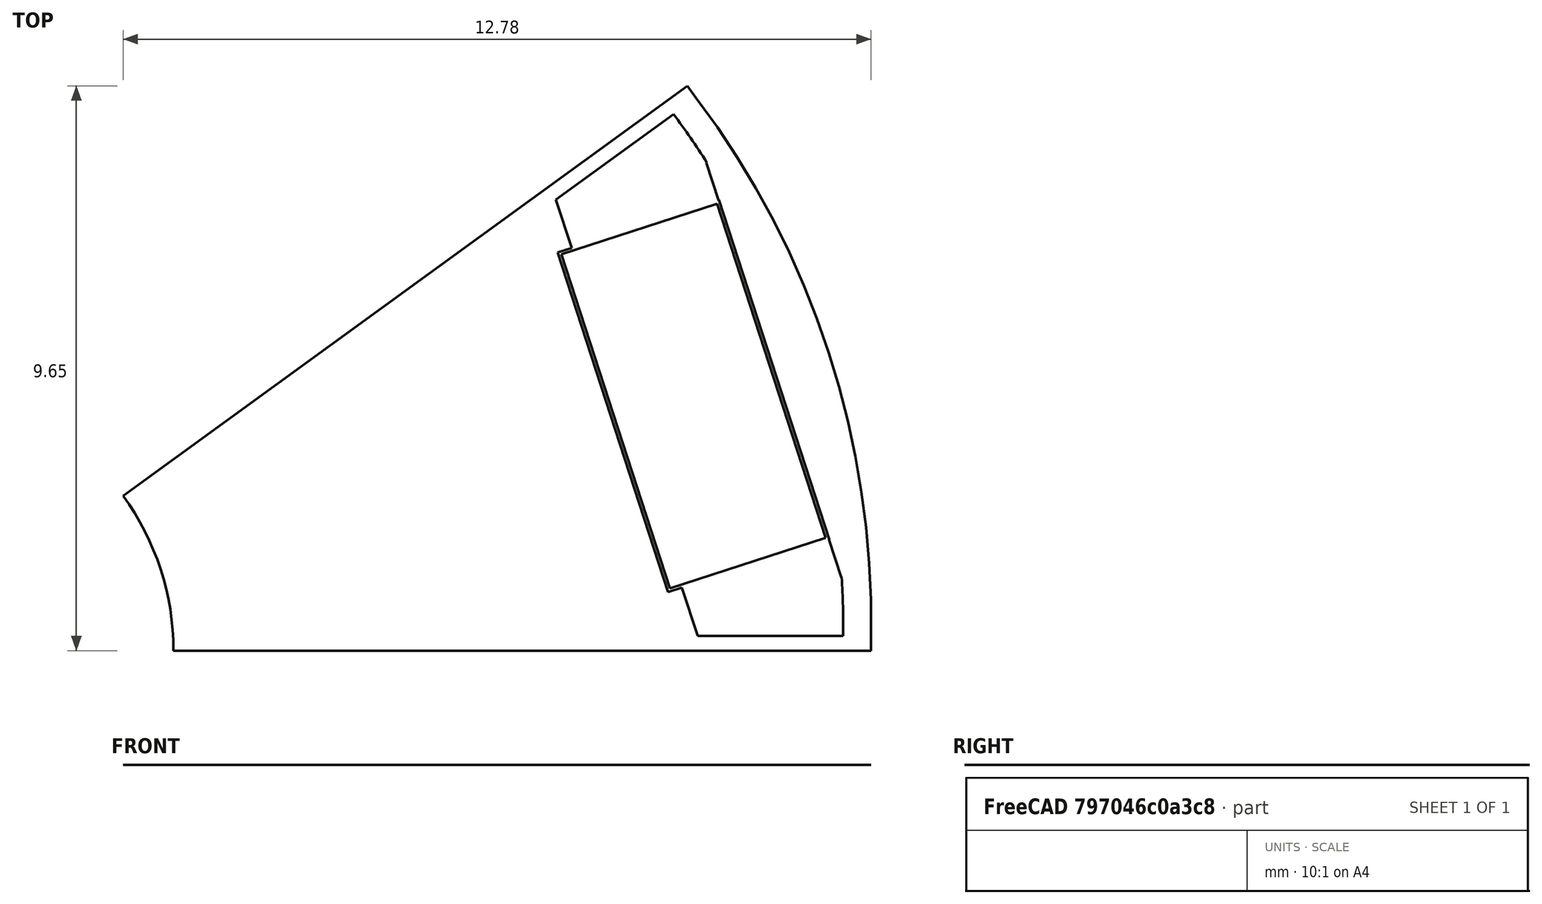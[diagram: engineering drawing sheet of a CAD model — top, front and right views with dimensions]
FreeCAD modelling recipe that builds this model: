
FCSTD DOCUMENT  (FreeCAD 0.18R4 (GitTag))
Label: rotor1
License: All rights reserved
LicenseURL: http://en.wikipedia.org/wiki/All_rights_reserved
objects: Sketcher::SketchObject×6, Surface::Filling×3, PartDesign::Body×2, Spreadsheet::Sheet×1, Part::Cut×1
note: 12 computed .brp shape members not serialized (recipe doc carries the construction recipe); baked Part::Feature solids carry a one-line shape summary decoded from their .brp

FEATURE [Spreadsheet::Sheet] Spreadsheet  label="Variables"
  cells = A2=poleNumber; B2(poleNumber)=10; A3=outerDiameter; B3(outerDiameter)=33; D3=Calc Value; A4=innerDiameter; B4(innerDiameter)=9; D4=Input Value; A5=stackLength; B5(stackLength)=20; A6=stackingFactor; B6(stackingFactor)=0.95; A7=embrace; B7(embrace)=75; A8=contourRatio; B8(contourRatio)=90; A9=magnetAirgap; B9(magnetAirgap)=0.05; A10=poleSeparation; B10(poleSeparation)=0.5; A11=magnetWidth; B11(magnetWidth)=6; A12=magnetHeight; B12(magnetHeight)=2.8; A13=rib; B13(rib)=0.5; A14=bridgeCurved; B14(bridgeCurved)=0.5; A15=cutTop; B15(cutTop)=0.01; A16=cutBottom; B16(cutBottom)=0.25; A17=segmentAngle; B17(segmentAngle)==360 / poleNumber; A18=movePocketInwards; B18(movePocketInwards)=0.01; A19=cuttingThickness; B19(cuttingThickness)=0.1; A20=magnetLength; B20(magnetLength)==stackLength; A21=cut; B21(cut)=0.2; A22=ribShaft; B22(ribShaft)=0.5; A23=magnetEmbrace; B23(magnetEmbrace)=70; A24=magnetContourRatio; B24(magnetContourRatio)=95; A25=axialMisalignment; B25(axialMisalignment)=0.5
FEATURE [Sketcher::SketchObject] Sketch003  label="RotorPoleSketch"
  MapMode = 5
  Support = -> [XY_Plane]
  expr: Constraints[14] = Variables.innerDiameter / 2
  expr: Constraints[55] = Variables.outerDiameter / 2 * Variables.contourRatio / 100
  expr: Constraints[73] = Variables.movePocketInwards
  expr: Constraints[59] = Variables.poleSeparation / 2
  expr: Constraints[106] = Variables.magnetHeight + 2 * Variables.magnetAirgap
  expr: Constraints[23] = Variables.outerDiameter / 2 * Variables.contourRatio / 100
  expr: Constraints[90] = Variables.cutTop
  expr: Constraints[71] = Variables.segmentAngle * Variables.embrace / 100
  expr: Constraints[15] = Variables.outerDiameter / 2
  expr: Constraints[103] = Variables.cutBottom
  expr: Constraints[58] = Variables.bridgeCurved
  expr: Constraints[114] = Variables.outerDiameter / 2 * Variables.contourRatio / 100 - Variables.bridgeCurved
  expr: Constraints[51] = Variables.rib / 2
  expr: Constraints[43] = Variables.rib / 2
  expr: Constraints[0] = Variables.segmentAngle
  expr: Constraints[18] = Variables.segmentAngle / 2
  expr: Constraints[91] = Variables.magnetWidth + Variables.magnetAirgap * 2
  expr: Constraints[116] = Variables.outerDiameter / 2 * Variables.contourRatio / 100 - Variables.bridgeCurved
  expr: Constraints[27] = Variables.poleSeparation / 2
  sketch-geometry (40):
    g0: LineSegment [constr] StartX=4.5 StartY=0 StartZ=0 EndX=16.5 EndY=0 EndZ=0
    g1: LineSegment [constr] StartX=3.64058 StartY=2.64503 StartZ=0 EndX=13.3488 EndY=9.69846 EndZ=0
    g2: LineSegment [constr] StartX=0 StartY=0 StartZ=0 EndX=4.5 EndY=0 EndZ=0
    g3: LineSegment [constr] StartX=0 StartY=0 StartZ=0 EndX=3.64058 EndY=2.64503 EndZ=0
    g4: ArcOfCircle [constr] CenterX=0 CenterY=0 CenterZ=0 NormalX=0 NormalY=0 NormalZ=1 AngleXU=0 Radius=16.5 StartAngle=0 EndAngle=0.628319
    g5: ArcOfCircle CenterX=0 CenterY=0 CenterZ=0 NormalX=0 NormalY=0 NormalZ=1 AngleXU=0 Radius=4.5 StartAngle=0 EndAngle=0.628319
    g6: LineSegment [constr] StartX=0 StartY=0 StartZ=0 EndX=15.6924 EndY=5.09878 EndZ=0
    g7: ArcOfCircle [constr] CenterX=1.56924 CenterY=0.509878 CenterZ=0 NormalX=0 NormalY=0 NormalZ=1 AngleXU=0 Radius=14.85 StartAngle=6.24884 EndAngle=6.94585
    g8: LineSegment StartX=13.2816 StartY=9.64965 StartZ=0 EndX=13.4286 EndY=9.4474 EndZ=0
    g9: LineSegment StartX=16.417 StartY=0 StartZ=0 EndX=16.417 EndY=0.25 EndZ=0
    g10: ArcOfCircle CenterX=1.56924 CenterY=0.509878 CenterZ=0 NormalX=0 NormalY=0 NormalZ=1 AngleXU=0 Radius=14.85 StartAngle=6.26568 EndAngle=6.929
    g11: LineSegment StartX=3.64058 StartY=2.64503 StartZ=0 EndX=13.2816 EndY=9.64965 EndZ=0
    g12: LineSegment StartX=4.5 StartY=0 StartZ=0 EndX=16.417 EndY=0 EndZ=0
    g13: LineSegment [constr] StartX=13.4942 StartY=9.49509 StartZ=0 EndX=3.7819 EndY=2.43869 EndZ=0
    g14: LineSegment [constr] StartX=3.7819 StartY=2.43869 StartZ=0 EndX=3.63495 EndY=2.64095 EndZ=0
    g15: LineSegment [constr] StartX=4.49305 StartY=0.25 StartZ=0 EndX=16.4981 EndY=0.25 EndZ=0
    g16: LineSegment [constr] StartX=4.49305 StartY=0.25 StartZ=0 EndX=4.49305 EndY=0 EndZ=0
    g17: ArcOfCircle [constr] CenterX=1.09371 CenterY=0.35537 CenterZ=0 NormalX=0 NormalY=0 NormalZ=1 AngleXU=0 Radius=14.85 StartAngle=6.25925 EndAngle=6.93544
    g18: LineSegment [constr] StartX=1.56924 StartY=0.509878 StartZ=0 EndX=1.09371 EndY=0.35537 EndZ=0
    g19: LineSegment [constr] StartX=15.9166 StartY=1.25266 StartZ=0 EndX=15.9066 EndY=1.25266 EndZ=0
    g20: LineSegment [constr] StartX=15.9066 StartY=1.25266 StartZ=0 EndX=13.605 EndY=8.33623 EndZ=0
    g21: LineSegment [constr] StartX=13.605 StartY=8.33623 StartZ=0 EndX=13.6131 EndY=8.34211 EndZ=0
    g22: LineSegment [constr] StartX=0 StartY=0 StartZ=0 EndX=15.9166 EndY=1.25266 EndZ=0
    g23: LineSegment [constr] StartX=0 StartY=0 StartZ=0 EndX=13.6131 EndY=8.34211 EndZ=0
    g24: ArcOfCircle [constr] CenterX=1.51524 CenterY=0.624283 CenterZ=0 NormalX=0 NormalY=0 NormalZ=1 AngleXU=0 Radius=14.35 StartAngle=0.567858 EndAngle=0.637767
    g25: ArcOfCircle [constr] CenterX=1.5928 CenterY=0.385581 CenterZ=0 NormalX=0 NormalY=0 NormalZ=1 AngleXU=0 Radius=14.35 StartAngle=6.27374 EndAngle=6.34365
    g26: LineSegment [constr] StartX=13.605 StartY=8.33623 StartZ=0 EndX=13.8133 EndY=7.69517 EndZ=0
    g27: LineSegment [constr] StartX=13.8133 StartY=7.69517 StartZ=0 EndX=13.8228 EndY=7.69826 EndZ=0
    g28: LineSegment [constr] StartX=13.8228 StartY=7.69826 StartZ=0 EndX=15.7078 EndY=1.89681 EndZ=0
    g29: LineSegment [constr] StartX=15.7078 StartY=1.89681 StartZ=0 EndX=15.6983 EndY=1.89372 EndZ=0
    g30: LineSegment [constr] StartX=15.6983 StartY=1.89372 StartZ=0 EndX=15.9066 EndY=1.25266 EndZ=0
    g31: LineSegment [constr] StartX=11.0335 StartY=7.70728 StartZ=0 EndX=13.4565 EndY=0.25 EndZ=0
    g32: LineSegment [constr] StartX=11.3025 StartY=6.87936 StartZ=0 EndX=11.0647 EndY=6.80211 EndZ=0
    g33: LineSegment [constr] StartX=11.0647 StartY=6.80211 StartZ=0 EndX=12.9497 EndY=1.00066 EndZ=0
    g34: LineSegment [constr] StartX=12.9497 StartY=1.00066 StartZ=0 EndX=13.1875 EndY=1.07792 EndZ=0
    g35: LineSegment [constr] StartX=12.9497 StartY=1.00066 StartZ=0 EndX=15.7078 EndY=1.89681 EndZ=0
    g36: LineSegment [constr] StartX=11.3025 StartY=6.87936 StartZ=0 EndX=11.0335 EndY=7.70728 EndZ=0
    g37: LineSegment [constr] StartX=13.1875 StartY=1.07792 StartZ=0 EndX=13.4565 EndY=0.25 EndZ=0
    g38: LineSegment [constr] StartX=11.0335 StartY=7.70728 StartZ=0 EndX=13.0444 EndY=9.16831 EndZ=0
    g39: LineSegment [constr] StartX=13.4565 StartY=0.25 StartZ=0 EndX=15.9422 EndY=0.25 EndZ=0
  constraints (117):
    c: Angle(g0,g1) = 0.628319
    c: Coincident(g2,g-1)
    c: Coincident(g2,g0)
    c: Coincident(g3,g2)
    c: Coincident(g3,g1)
    c: Parallel(g2,g0)
    c: Parallel(g3,g1)
    c: Coincident(g4,g-1)
    c: Coincident(g4,g0)
    c: Coincident(g4,g1)
    c: Coincident(g5,g4)
    c: Coincident(g5,g1)
    c: Coincident(g5,g0)
    c: Angle(g-1,g2) = 0
    c: Radius(g5) = 4.5
    c: Radius(g4) = 16.5
    c: Coincident(g6,g5)
    c: PointOnObject(g6,g4)
    c: Angle(g-1,g6) = 0.314159
    c: PointOnObject(g7,g1)
    c: PointOnObject(g7,g0)
    c: PointOnObject(g6,g7)
    c: PointOnObject(g7,g6)
    c: Radius(g7) = 14.85
    c: PointOnObject(g8,g1)
    c: PointOnObject(g8,g7)
    c: Angle(g1,g8) = 1.5708
    c: Distance(g8) = 0.25
    c: PointOnObject(g9,g0)
    c: PointOnObject(g9,g7)
    c: Angle(g9,g0) = 1.5708
    c: Coincident(g10,g8)
    c: Coincident(g10,g9)
    c: PointOnObject(g6,g10)
    c: Coincident(g11,g5)
    c: Coincident(g11,g8)
    c: Coincident(g12,g5)
    c: Coincident(g12,g9)
    c: PointOnObject(g13,g4)
    c: PointOnObject(g13,g5)
    c: Coincident(g14,g13)
    c: PointOnObject(g14,g11)
    c: Angle(g13,g14) = 1.5708
    c: Distance(g14) = 0.25
    c: Parallel(g11,g13)
    c: PointOnObject(g15,g5)
    c: PointOnObject(g15,g4)
    c: Parallel(g15,g2)
    c: Coincident(g16,g15)
    c: PointOnObject(g16,g2)
    c: Angle(g16,g15) = 1.5708
    c: Distance(g16) = 0.25
    c: PointOnObject(g17,g6)
    c: PointOnObject(g17,g11)
    c: PointOnObject(g17,g12)
    c: Radius(g17) = 14.85
    c: Coincident(g18,g10)
    c: Coincident(g18,g17)
    c: Distance(g17,g10) = 0.5
    c: DistanceY(g9,g9) = 0.25
    c: PointOnObject(g38,g13)
    c: PointOnObject(g39,g15)
    c: PointOnObject(g19,g17)
    c: Horizontal(g19)
    c: Coincident(g20,g19)
    c: Coincident(g21,g20)
    c: Coincident(g22,g5)
    c: Coincident(g22,g19)
    c: Coincident(g23,g5)
    c: Coincident(g23,g21)
    c: Symmetric(g21,g19,g6)
    c: Angle(g22,g23) = 0.471239
    c: Parallel(g21,g11)
    c: DistanceX(g19,g19) = 0.01
    c: Equal(g19,g21)
    c: Coincident(g24,g21)
    c: Tangent(g24,g17)
    c: Coincident(g25,g19)
    c: Tangent(g25,g17)
    c: Coincident(g26,g21)
    c: PointOnObject(g26,g20)
    c: Coincident(g27,g26)
    c: Coincident(g28,g27)
    c: Coincident(g29,g28)
    c: Coincident(g30,g29)
    c: Coincident(g30,g19)
    c: Angle(g29,g20) = 1.5708
    c: Perpendicular(g29,g28)
    c: Angle(g27,g28) = 1.5708
    c: Symmetric(g29,g26,g6)
    c: Distance(g27) = 0.01
    c: Distance(g28) = 6.1
    c: PointOnObject(g31,g13)
    c: PointOnObject(g31,g15)
    c: Parallel(g31,g20)
    c: PointOnObject(g32,g31)
    c: Coincident(g33,g32)
    c: Coincident(g34,g33)
    c: PointOnObject(g34,g31)
    c: Angle(g33,g32) = 1.5708
    c: Angle(g34,g33) = 1.5708
    c: Symmetric(g32,g33,g6)
    c: Equal(g33,g28)
    c: Distance(g34) = 0.25
    c: Coincident(g35,g33)
    c: Coincident(g35,g28)
    c: Distance(g35) = 2.9
    c: Coincident(g36,g32)
    c: Coincident(g36,g31)
    c: Coincident(g37,g34)
    c: Coincident(g37,g31)
    c: Coincident(g38,g36)
    c: Coincident(g39,g37)
    c: Coincident(g24,g38)
    c: Radius(g24) = 14.35
    c: Coincident(g25,g39)
    c: Radius(g25) = 14.35
FEATURE [Sketcher::SketchObject] Sketch004  label="BoundingBox"
  MapMode = 5
  Support = -> [XY_Plane]
  expr: Constraints[8] = Variables.outerDiameter
  sketch-geometry (6):
    g0: LineSegment StartX=-16.5 StartY=-16.5 StartZ=0 EndX=16.5 EndY=-16.5 EndZ=0
    g1: LineSegment StartX=16.5 StartY=-16.5 StartZ=0 EndX=16.5 EndY=16.5 EndZ=0
    g2: LineSegment StartX=16.5 StartY=16.5 StartZ=0 EndX=-16.5 EndY=16.5 EndZ=0
    g3: LineSegment StartX=-16.5 StartY=16.5 StartZ=0 EndX=-16.5 EndY=-16.5 EndZ=0
    g4: LineSegment [constr] StartX=-16.5 StartY=-16.5 StartZ=0 EndX=16.5 EndY=16.5 EndZ=0
    g5: GeomPoint X=0 Y=0 Z=0
  constraints (14):
    c: Coincident(g0,g1)
    c: Coincident(g1,g2)
    c: Coincident(g2,g3)
    c: Coincident(g3,g0)
    c: Horizontal(g0)
    c: Horizontal(g2)
    c: Vertical(g1)
    c: Vertical(g3)
    c: DistanceY(g1,g1) = 33
    c: Equal(g2,g1)
    c: Coincident(g4,g0)
    c: Coincident(g4,g1)
    c: Symmetric(g0,g1,g5)
    c: Coincident(g-1,g5)
FEATURE [Sketcher::SketchObject] Sketch005  label="RotorSideSketch"
  MapMode = 5
  Support = -> [XY_Plane001]
  expr: Constraints[23] = Variables.stackLength / 2 - Variables.axialMisalignment
  expr: Constraints[19] = Variables.innerDiameter / 2
  expr: Constraints[22] = Variables.stackLength / 2 - Variables.axialMisalignment
  expr: Constraints[9] = Variables.outerDiameter / 2
  expr: Constraints[8] = Variables.innerDiameter / 2
  expr: Constraints[7] = Variables.stackLength
  sketch-geometry (8):
    g0: LineSegment StartX=-9.5 StartY=4.5 StartZ=0 EndX=10.5 EndY=4.5 EndZ=0
    g1: LineSegment StartX=10.5 StartY=4.5 StartZ=0 EndX=10.5 EndY=16.5 EndZ=0
    g2: LineSegment StartX=10.5 StartY=16.5 StartZ=0 EndX=-9.5 EndY=16.5 EndZ=0
    g3: LineSegment StartX=-9.5 StartY=16.5 StartZ=0 EndX=-9.5 EndY=4.5 EndZ=0
    g4: LineSegment StartX=-9.5 StartY=-4.5 StartZ=0 EndX=10.5 EndY=-4.5 EndZ=0
    g5: LineSegment StartX=10.5 StartY=-4.5 StartZ=0 EndX=10.5 EndY=-16.5 EndZ=0
    g6: LineSegment StartX=10.5 StartY=-16.5 StartZ=0 EndX=-9.5 EndY=-16.5 EndZ=0
    g7: LineSegment StartX=-9.5 StartY=-16.5 StartZ=0 EndX=-9.5 EndY=-4.5 EndZ=0
  constraints (24):
    c: Coincident(g0,g1)
    c: Coincident(g1,g2)
    c: Coincident(g2,g3)
    c: Coincident(g3,g0)
    c: Horizontal(g0)
    c: Vertical(g1)
    c: Vertical(g3)
    c: DistanceX(g2,g2) = 20
    c: DistanceY(g-1,g0) = 4.5
    c: DistanceY(g-1,g1) = 16.5
    c: Coincident(g4,g5)
    c: Coincident(g5,g6)
    c: Coincident(g6,g7)
    c: Coincident(g7,g4)
    c: Horizontal(g4)
    c: Vertical(g5)
    c: Vertical(g7)
    c: Equal(g4,g0)
    c: Equal(g7,g3)
    c: DistanceY(g4,g-1) = 4.5
    c: Horizontal(g2)
    c: Horizontal(g6)
    c: DistanceX(g0,g-1) = 9.5
    c: DistanceX(g4,g-1) = 9.5
FEATURE [Sketcher::SketchObject] Sketch006  label="MagnetSideSketch"
  ExternalGeometry = -> [Sketch005]
  MapMode = 5
  Support = -> [XY_Plane001]
  expr: Constraints[23] = Variables.stackLength / 2 - Variables.axialMisalignment
  expr: Constraints[12] = Variables.magnetHeight / 2
  expr: Constraints[8] = Variables.magnetHeight
  expr: Constraints[7] = Variables.magnetLength
  sketch-geometry (9):
    g0: LineSegment StartX=-9.5 StartY=12.3 StartZ=0 EndX=10.5 EndY=12.3 EndZ=0
    g1: LineSegment StartX=10.5 StartY=12.3 StartZ=0 EndX=10.5 EndY=15.1 EndZ=0
    g2: LineSegment StartX=10.5 StartY=15.1 StartZ=0 EndX=-9.5 EndY=15.1 EndZ=0
    g3: LineSegment StartX=-9.5 StartY=15.1 StartZ=0 EndX=-9.5 EndY=12.3 EndZ=0
    g4: LineSegment [constr] StartX=10.5 StartY=15.1 StartZ=0 EndX=10.5 EndY=16.5 EndZ=0
    g5: LineSegment StartX=-9.5 StartY=-15.1 StartZ=0 EndX=10.5 EndY=-15.1 EndZ=0
    g6: LineSegment StartX=10.5 StartY=-15.1 StartZ=0 EndX=10.5 EndY=-12.3 EndZ=0
    g7: LineSegment StartX=10.5 StartY=-12.3 StartZ=0 EndX=-9.5 EndY=-12.3 EndZ=0
    g8: LineSegment StartX=-9.5 StartY=-12.3 StartZ=0 EndX=-9.5 EndY=-15.1 EndZ=0
  constraints (25):
    c: Coincident(g0,g1)
    c: Coincident(g1,g2)
    c: Coincident(g2,g3)
    c: Coincident(g3,g0)
    c: Horizontal(g0)
    c: Vertical(g1)
    c: Vertical(g3)
    c: DistanceX(g2,g2) = 20
    c: DistanceY(g1,g1) = 2.8
    c: Coincident(g4,g1)
    c: PointOnObject(g4,g-3)
    c: Angle(g4,g2) = 1.5708
    c: DistanceY(g4,g4) = 1.4
    c: Coincident(g5,g6)
    c: Coincident(g6,g7)
    c: Coincident(g7,g8)
    c: Coincident(g8,g5)
    c: Horizontal(g5)
    c: Vertical(g6)
    c: Vertical(g8)
    c: Symmetric(g7,g0,g-1)
    c: Symmetric(g6,g0,g-1)
    c: Equal(g8,g3)
    c: DistanceX(g0,g-1) = 9.5
    c: Horizontal(g2)
FEATURE [PartDesign::Body] Body001  label="SideView"
  Group = -> [Sketch005,Sketch006]
  Origin = -> Origin001
FEATURE [Surface::Filling] Surface  label="RotorPoleSketch_Surface"
  Anisotropy = false
  BoundaryEdges = -> [Sketch003]
  BoundaryOrder = [0,0,0,0,0,0]
  Degree = 3
  Iterations = 2
  MaximumDegree = 8
  MaximumSegments = 9
  PointsOnCurve = 15
  TolAngular = 0.01
  TolCurvature = 0.1
  Tolerance2d = 1e-05
  Tolerance3d = 0.0001
FEATURE [Sketcher::SketchObject] Sketch007  label="PocketSketch"
  MapMode = 5
  Support = -> [XY_Plane]
  expr: Constraints[14] = Variables.innerDiameter / 2
  expr: Constraints[55] = Variables.outerDiameter / 2 * Variables.contourRatio / 100
  expr: Constraints[73] = Variables.movePocketInwards
  expr: Constraints[59] = Variables.poleSeparation / 2
  expr: Constraints[106] = Variables.magnetHeight + 2 * Variables.magnetAirgap
  expr: Constraints[23] = Variables.outerDiameter / 2 * Variables.contourRatio / 100
  expr: Constraints[90] = Variables.cutTop
  expr: Constraints[71] = Variables.segmentAngle * Variables.embrace / 100
  expr: Constraints[15] = Variables.outerDiameter / 2
  expr: Constraints[103] = Variables.cutBottom
  expr: Constraints[58] = Variables.bridgeCurved
  expr: Constraints[114] = Variables.outerDiameter / 2 * Variables.contourRatio / 100 - Variables.bridgeCurved
  expr: Constraints[51] = Variables.rib / 2
  expr: Constraints[43] = Variables.rib / 2
  expr: Constraints[18] = Variables.segmentAngle / 2
  expr: Constraints[0] = Variables.segmentAngle
  expr: Constraints[91] = Variables.magnetWidth + Variables.magnetAirgap * 2
  expr: Constraints[116] = Variables.outerDiameter / 2 * Variables.contourRatio / 100 - Variables.bridgeCurved
  expr: Constraints[27] = Variables.poleSeparation / 2
  sketch-geometry (40):
    g0: LineSegment [constr] StartX=4.5 StartY=0 StartZ=0 EndX=16.5 EndY=0 EndZ=0
    g1: LineSegment [constr] StartX=3.64058 StartY=2.64503 StartZ=0 EndX=13.3488 EndY=9.69846 EndZ=0
    g2: LineSegment [constr] StartX=0 StartY=0 StartZ=0 EndX=4.5 EndY=0 EndZ=0
    g3: LineSegment [constr] StartX=0 StartY=0 StartZ=0 EndX=3.64058 EndY=2.64503 EndZ=0
    g4: ArcOfCircle [constr] CenterX=0 CenterY=0 CenterZ=0 NormalX=0 NormalY=0 NormalZ=1 AngleXU=0 Radius=16.5 StartAngle=0 EndAngle=0.628319
    g5: ArcOfCircle [constr] CenterX=0 CenterY=0 CenterZ=0 NormalX=0 NormalY=0 NormalZ=1 AngleXU=0 Radius=4.5 StartAngle=0 EndAngle=0.628319
    g6: LineSegment [constr] StartX=0 StartY=0 StartZ=0 EndX=15.6924 EndY=5.09878 EndZ=0
    g7: ArcOfCircle [constr] CenterX=1.56924 CenterY=0.509878 CenterZ=0 NormalX=0 NormalY=0 NormalZ=1 AngleXU=0 Radius=14.85 StartAngle=6.24884 EndAngle=6.94585
    g8: LineSegment [constr] StartX=13.2816 StartY=9.64965 StartZ=0 EndX=13.4286 EndY=9.4474 EndZ=0
    g9: LineSegment [constr] StartX=16.417 StartY=0 StartZ=0 EndX=16.417 EndY=0.25 EndZ=0
    g10: ArcOfCircle [constr] CenterX=1.56924 CenterY=0.509878 CenterZ=0 NormalX=0 NormalY=0 NormalZ=1 AngleXU=0 Radius=14.85 StartAngle=6.26568 EndAngle=6.929
    g11: LineSegment [constr] StartX=3.64058 StartY=2.64503 StartZ=0 EndX=13.2816 EndY=9.64965 EndZ=0
    g12: LineSegment [constr] StartX=4.5 StartY=0 StartZ=0 EndX=16.417 EndY=0 EndZ=0
    g13: LineSegment [constr] StartX=13.4942 StartY=9.49509 StartZ=0 EndX=3.7819 EndY=2.43869 EndZ=0
    g14: LineSegment [constr] StartX=3.7819 StartY=2.43869 StartZ=0 EndX=3.63495 EndY=2.64095 EndZ=0
    g15: LineSegment [constr] StartX=4.49305 StartY=0.25 StartZ=0 EndX=16.4981 EndY=0.25 EndZ=0
    g16: LineSegment [constr] StartX=4.49305 StartY=0.25 StartZ=0 EndX=4.49305 EndY=0 EndZ=0
    g17: ArcOfCircle [constr] CenterX=1.09371 CenterY=0.35537 CenterZ=0 NormalX=0 NormalY=0 NormalZ=1 AngleXU=0 Radius=14.85 StartAngle=6.25925 EndAngle=6.93544
    g18: LineSegment [constr] StartX=1.56924 StartY=0.509878 StartZ=0 EndX=1.09371 EndY=0.35537 EndZ=0
    g19: LineSegment StartX=15.9166 StartY=1.25266 StartZ=0 EndX=15.9066 EndY=1.25266 EndZ=0
    g20: LineSegment [constr] StartX=15.9066 StartY=1.25266 StartZ=0 EndX=13.605 EndY=8.33623 EndZ=0
    g21: LineSegment StartX=13.605 StartY=8.33623 StartZ=0 EndX=13.6131 EndY=8.34211 EndZ=0
    g22: LineSegment [constr] StartX=0 StartY=0 StartZ=0 EndX=15.9166 EndY=1.25266 EndZ=0
    g23: LineSegment [constr] StartX=0 StartY=0 StartZ=0 EndX=13.6131 EndY=8.34211 EndZ=0
    g24: ArcOfCircle CenterX=1.51524 CenterY=0.624283 CenterZ=0 NormalX=0 NormalY=0 NormalZ=1 AngleXU=0 Radius=14.35 StartAngle=0.567858 EndAngle=0.637767
    g25: ArcOfCircle CenterX=1.5928 CenterY=0.385581 CenterZ=0 NormalX=0 NormalY=0 NormalZ=1 AngleXU=0 Radius=14.35 StartAngle=6.27374 EndAngle=6.34365
    g26: LineSegment StartX=13.605 StartY=8.33623 StartZ=0 EndX=13.8133 EndY=7.69517 EndZ=0
    g27: LineSegment StartX=13.8133 StartY=7.69517 StartZ=0 EndX=13.8228 EndY=7.69826 EndZ=0
    g28: LineSegment StartX=13.8228 StartY=7.69826 StartZ=0 EndX=15.7078 EndY=1.89681 EndZ=0
    g29: LineSegment StartX=15.7078 StartY=1.89681 StartZ=0 EndX=15.6983 EndY=1.89372 EndZ=0
    g30: LineSegment StartX=15.6983 StartY=1.89372 StartZ=0 EndX=15.9066 EndY=1.25266 EndZ=0
    g31: LineSegment [constr] StartX=11.0335 StartY=7.70728 StartZ=0 EndX=13.4565 EndY=0.25 EndZ=0
    g32: LineSegment StartX=11.3025 StartY=6.87936 StartZ=0 EndX=11.0647 EndY=6.80211 EndZ=0
    g33: LineSegment StartX=11.0647 StartY=6.80211 StartZ=0 EndX=12.9497 EndY=1.00066 EndZ=0
    g34: LineSegment StartX=12.9497 StartY=1.00066 StartZ=0 EndX=13.1875 EndY=1.07792 EndZ=0
    g35: LineSegment [constr] StartX=12.9497 StartY=1.00066 StartZ=0 EndX=15.7078 EndY=1.89681 EndZ=0
    g36: LineSegment StartX=11.3025 StartY=6.87936 StartZ=0 EndX=11.0335 EndY=7.70728 EndZ=0
    g37: LineSegment StartX=13.1875 StartY=1.07792 StartZ=0 EndX=13.4565 EndY=0.25 EndZ=0
    g38: LineSegment StartX=11.0335 StartY=7.70728 StartZ=0 EndX=13.0444 EndY=9.16831 EndZ=0
    g39: LineSegment StartX=13.4565 StartY=0.25 StartZ=0 EndX=15.9422 EndY=0.25 EndZ=0
  constraints (117):
    c: Angle(g0,g1) = 0.628319
    c: Coincident(g2,g-1)
    c: Coincident(g2,g0)
    c: Coincident(g3,g2)
    c: Coincident(g3,g1)
    c: Parallel(g2,g0)
    c: Parallel(g3,g1)
    c: Coincident(g4,g-1)
    c: Coincident(g4,g0)
    c: Coincident(g4,g1)
    c: Coincident(g5,g4)
    c: Coincident(g5,g1)
    c: Coincident(g5,g0)
    c: Angle(g-1,g2) = 0
    c: Radius(g5) = 4.5
    c: Radius(g4) = 16.5
    c: Coincident(g6,g5)
    c: PointOnObject(g6,g4)
    c: Angle(g-1,g6) = 0.314159
    c: PointOnObject(g7,g1)
    c: PointOnObject(g7,g0)
    c: PointOnObject(g6,g7)
    c: PointOnObject(g7,g6)
    c: Radius(g7) = 14.85
    c: PointOnObject(g8,g1)
    c: PointOnObject(g8,g7)
    c: Angle(g1,g8) = 1.5708
    c: Distance(g8) = 0.25
    c: PointOnObject(g9,g0)
    c: PointOnObject(g9,g7)
    c: Angle(g9,g0) = 1.5708
    c: Coincident(g10,g8)
    c: Coincident(g10,g9)
    c: PointOnObject(g6,g10)
    c: Coincident(g11,g5)
    c: Coincident(g11,g8)
    c: Coincident(g12,g5)
    c: Coincident(g12,g9)
    c: PointOnObject(g13,g4)
    c: PointOnObject(g13,g5)
    c: Coincident(g14,g13)
    c: PointOnObject(g14,g11)
    c: Angle(g13,g14) = 1.5708
    c: Distance(g14) = 0.25
    c: Parallel(g11,g13)
    c: PointOnObject(g15,g5)
    c: PointOnObject(g15,g4)
    c: Parallel(g15,g2)
    c: Coincident(g16,g15)
    c: PointOnObject(g16,g2)
    c: Angle(g16,g15) = 1.5708
    c: Distance(g16) = 0.25
    c: PointOnObject(g17,g6)
    c: PointOnObject(g17,g11)
    c: PointOnObject(g17,g12)
    c: Radius(g17) = 14.85
    c: Coincident(g18,g10)
    c: Coincident(g18,g17)
    c: Distance(g17,g10) = 0.5
    c: DistanceY(g9,g9) = 0.25
    c: PointOnObject(g38,g13)
    c: PointOnObject(g39,g15)
    c: PointOnObject(g19,g17)
    c: Horizontal(g19)
    c: Coincident(g20,g19)
    c: Coincident(g21,g20)
    c: Coincident(g22,g5)
    c: Coincident(g22,g19)
    c: Coincident(g23,g5)
    c: Coincident(g23,g21)
    c: Symmetric(g21,g19,g6)
    c: Angle(g22,g23) = 0.471239
    c: Parallel(g21,g11)
    c: DistanceX(g19,g19) = 0.01
    c: Equal(g19,g21)
    c: Coincident(g24,g21)
    c: Tangent(g24,g17)
    c: Coincident(g25,g19)
    c: Tangent(g25,g17)
    c: Coincident(g26,g21)
    c: PointOnObject(g26,g20)
    c: Coincident(g27,g26)
    c: Coincident(g28,g27)
    c: Coincident(g29,g28)
    c: Coincident(g30,g29)
    c: Coincident(g30,g19)
    c: Angle(g29,g20) = 1.5708
    c: Perpendicular(g29,g28)
    c: Angle(g27,g28) = 1.5708
    c: Symmetric(g29,g26,g6)
    c: Distance(g27) = 0.01
    c: Distance(g28) = 6.1
    c: PointOnObject(g31,g13)
    c: PointOnObject(g31,g15)
    c: Parallel(g31,g20)
    c: PointOnObject(g32,g31)
    c: Coincident(g33,g32)
    c: Coincident(g34,g33)
    c: PointOnObject(g34,g31)
    c: Angle(g33,g32) = 1.5708
    c: Angle(g34,g33) = 1.5708
    c: Symmetric(g32,g33,g6)
    c: Equal(g33,g28)
    c: Distance(g34) = 0.25
    c: Coincident(g35,g33)
    c: Coincident(g35,g28)
    c: Distance(g35) = 2.9
    c: Coincident(g36,g32)
    c: Coincident(g36,g31)
    c: Coincident(g37,g34)
    c: Coincident(g37,g31)
    c: Coincident(g38,g36)
    c: Coincident(g39,g37)
    c: Coincident(g24,g38)
    c: Radius(g24) = 14.35
    c: Coincident(g25,g39)
    c: Radius(g25) = 14.35
FEATURE [Sketcher::SketchObject] Sketch  label="MagnetSketch"
  ExternalGeometry = -> [Sketch007]
  MapMode = 5
  Support = -> [XY_Plane]
  expr: Constraints[14] = Variables.magnetAirgap
  expr: Constraints[8] = Variables.magnetHeight
  expr: Constraints[7] = Variables.magnetWidth
  sketch-geometry (6):
    g0: LineSegment StartX=11.1277 StartY=6.77001 StartZ=0 EndX=13.7907 EndY=7.63525 EndZ=0
    g1: LineSegment StartX=13.7907 StartY=7.63525 StartZ=0 EndX=15.6448 EndY=1.92892 EndZ=0
    g2: LineSegment StartX=15.6448 StartY=1.92892 StartZ=0 EndX=12.9818 EndY=1.06367 EndZ=0
    g3: LineSegment StartX=12.9818 StartY=1.06367 StartZ=0 EndX=11.1277 EndY=6.77001 EndZ=0
    g4: LineSegment [constr] StartX=11.1277 StartY=6.77001 StartZ=0 EndX=11.1123 EndY=6.81756 EndZ=0
    g5: LineSegment [constr] StartX=11.1277 StartY=6.77001 StartZ=0 EndX=11.0802 EndY=6.75456 EndZ=0
  constraints (18):
    c: Coincident(g1,g0)
    c: Coincident(g2,g1)
    c: Coincident(g3,g2)
    c: Coincident(g3,g0)
    c: Angle(g3,g0) = 1.5708
    c: Parallel(g0,g2)
    c: Parallel(g3,g1)
    c: Distance(g3) = 6
    c: Distance(g2) = 2.8
    c: Coincident(g4,g0)
    c: Coincident(g5,g0)
    c: Angle(g0,g4) = 1.5708
    c: Angle(g5,g3) = 1.5708
    c: Equal(g5,g4)
    c: Distance(g4) = 0.05
    c: PointOnObject(g4,g-3)
    c: PointOnObject(g5,g-4)
    c: Parallel(g3,g-4)
FEATURE [PartDesign::Body] Body  label="TopView"
  Group = -> [Sketch003,Sketch004,Sketch,Sketch007]
  Origin = -> Origin
FEATURE [Surface::Filling] Surface001  label="PocketSketch_Surface"
  Anisotropy = false
  BoundaryEdges = -> [Sketch007]
  BoundaryOrder = [0,0,0,0,0,0,0,0,0,0,0,0,0,0,0,0]
  Degree = 3
  Iterations = 2
  MaximumDegree = 8
  MaximumSegments = 9
  PointsOnCurve = 15
  TolAngular = 0.01
  TolCurvature = 0.1
  Tolerance2d = 1e-05
  Tolerance3d = 0.0001
FEATURE [Part::Cut] Cut  label="Rotor_Surface"
  Base = -> Surface
  Tool = -> Surface001
FEATURE [Surface::Filling] Surface002  label="Magnet_Surface"
  Anisotropy = false
  BoundaryEdges = -> [Sketch]
  BoundaryOrder = [0,0,0,0]
  Degree = 3
  Iterations = 2
  MaximumDegree = 8
  MaximumSegments = 9
  PointsOnCurve = 15
  TolAngular = 0.01
  TolCurvature = 0.1
  Tolerance2d = 1e-05
  Tolerance3d = 0.0001
